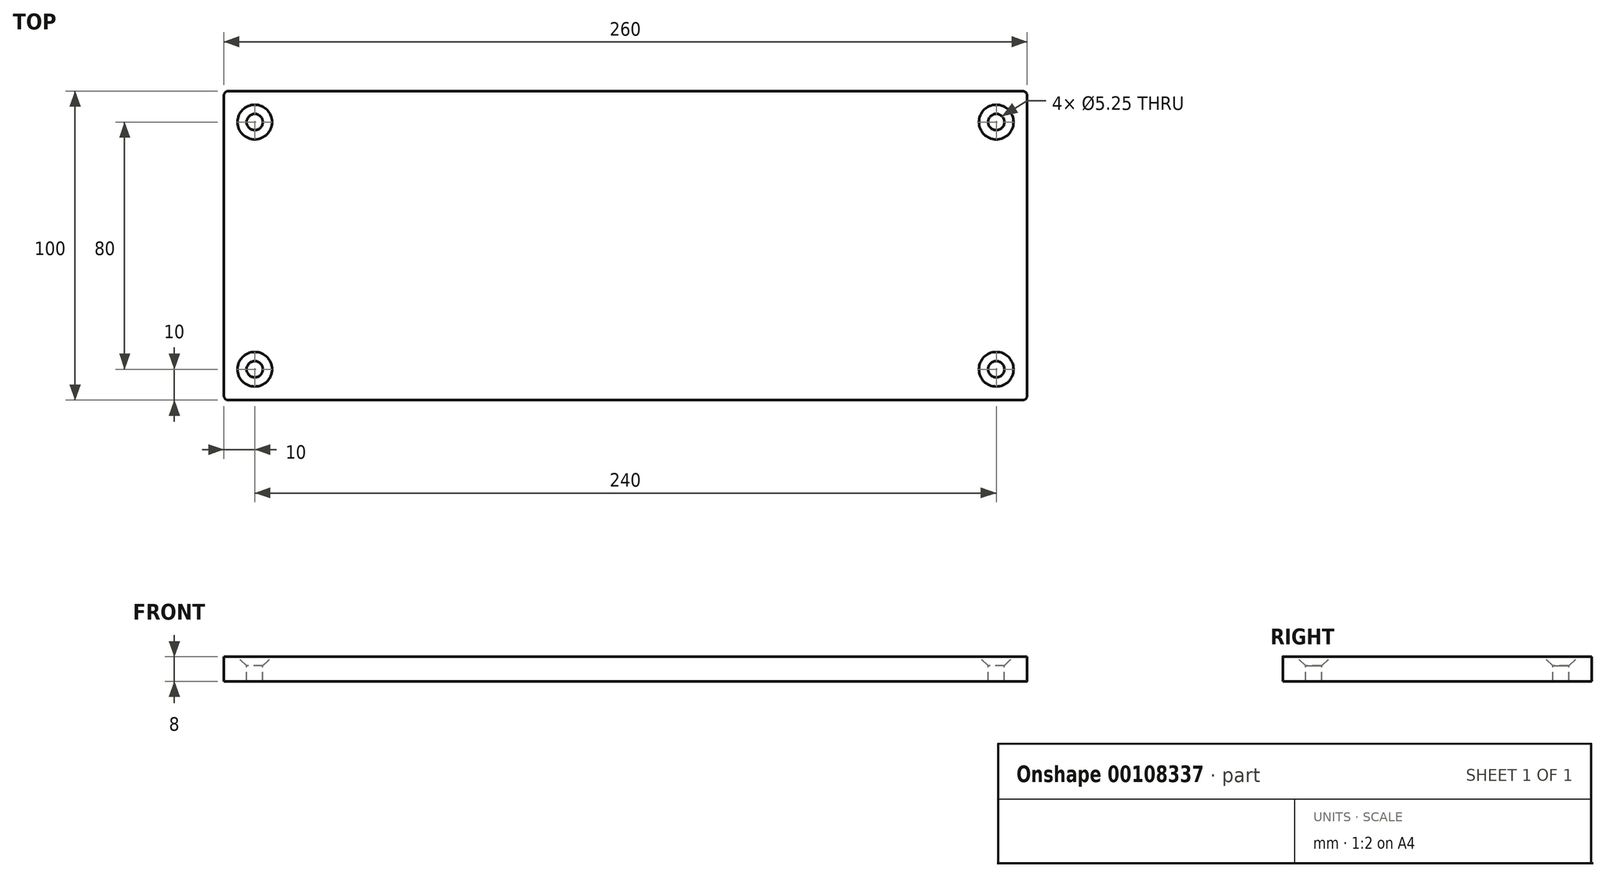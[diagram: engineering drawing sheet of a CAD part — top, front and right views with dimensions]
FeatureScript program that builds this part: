
annotation { "Feature Type Name" : "Feature", "Feature Type Description" : "" }
export const myFeature = defineFeature(function(context is Context, id is Id, definition is map)
    precondition{}
    {
        {
            var Q0;
            Q0=qCreatedBy(makeId("Top.planeOp"),FACE);
            var sketch = newSketch(context, id + "F0", { "sketchPlane" : qUnion([Q0])});
            skLineSegment(sketch, "E0.bottom", {"start": v(0, 0) * mm, "end": v(-260, 0) * mm});
            skLineSegment(sketch, "E0.top", {"start": v(0, 100) * mm, "end": v(-260, 100) * mm});
            skLineSegment(sketch, "E0.left", {"start": v(0, 0) * mm, "end": v(0, 100) * mm});
            skLineSegment(sketch, "E0.right", {"start": v(-260, 0) * mm, "end": v(-260, 100) * mm});
            skLineSegment(sketch, "E1", {"start": v(-260, 50) * mm, "end": v(0, 50) * mm, "construction": true});
            skLineSegment(sketch, "E2", {"start": v(-130, 100) * mm, "end": v(-130, 0) * mm, "construction": true});
            skPoint(sketch, "E3", {"position": v(-250, 10) * mm});
            skPoint(sketch, "E4.MirrorP", {"position": v(-250, 90) * mm});
            skPoint(sketch, "E5.MirrorP", {"position": v(-10, 90) * mm});
            skPoint(sketch, "E6.MirrorP", {"position": v(-10, 10) * mm});
            skSolve(sketch);
        }
        {
            var Q0;
            Q0=makeQuery(id+"F0.imprint","IMPRINT",FACE,{"disambiguationData":[TD([[makeQuery(id+"F0.imprint","IMPRINT",EDGE,{"derivedFrom":sQuery(id+"F0.wireOp",EDGE,"E0.bottom")}),-1.0]])]});
            extrude(context, id + "F1", {"entities" : qUnion([Q0]), "oppositeDirection" : true, "depth" : 8 * mm});
        }
        {
            var Q0;
            Q0=sQuery(id+"F0.wireOp",VERTEX,"E3");
            var Q1;
            Q1=sQuery(id+"F0.wireOp",VERTEX,"cffc4b24-a0ba-456e-b655-3c8573d52c1b");
            var Q2;
            Q2=sQuery(id+"F0.wireOp",VERTEX,"e33c571e-dceb-4edd-b5c1-62c351230e5a2.MirrorP");
            var Q3;
            Q3=sQuery(id+"F0.wireOp",VERTEX,"E6.MirrorP");
            var Q4;
            Q4=sQuery(id+"F0.wireOp",VERTEX,"e33c571e-dceb-4edd-b5c1-62c351230e5a3.MirrorP");
            var Q5;
            Q5=sQuery(id+"F0.wireOp",VERTEX,"E5.MirrorP");
            var Q6;
            Q6=sQuery(id+"F0.wireOp",VERTEX,"E4.MirrorP");
            var Q7;
            Q7=sQuery(id+"F0.wireOp",VERTEX,"1f4b834b-5920-4e6c-9070-407c551c4e2a0.MirrorP");
            var Q8;
            Q8=makeQuery(id+"F1.opExtrude","SWEPT_BODY",BODY,{"disambiguationData":[OSD([sQuery(id+"F0.wireOp",EDGE,"E0.bottom"),sQuery(id+"F0.wireOp",EDGE,"E0.top"),sQuery(id+"F0.wireOp",EDGE,"E0.left"),sQuery(id+"F0.wireOp",EDGE,"E0.right")])]});
            hole(context, id + "F2", {"style" : HoleStyle.C_SINK, "endStyle" : HoleEndStyle.THROUGH, "standardTappedOrClearance" : lookupTablePath({ "standard" : "ISO", "fit" : "Close", "size" : "M5", "type" : "Clearance" }), "standardBlindInLast" : lookupTablePath({ "fit" : "Close", "standard" : "ISO", "size" : "M5", "type" : "Clearance" }), "holeDiameter" : 5.25 * mm, "cSinkDiameter" : 11.2 * mm, "cSinkAngle" : 90 * degree, "locations" : qUnion([Q0, Q1, Q2, Q3, Q4, Q5, Q6, Q7]), "scope" : qUnion([Q8]), "isTappedThrough" : true});
        }
        {
            var Q0;
            Q0=makeQuery(id+"F1.opExtrude","SWEPT_EDGE",EDGE,{"disambiguationData":[OSD([sQuery(id+"F0.wireOp",EDGE,"E0.bottom"),sQuery(id+"F0.wireOp",EDGE,"E0.left")])]});
            var Q1;
            Q1=makeQuery(id+"F1.opExtrude","SWEPT_EDGE",EDGE,{"disambiguationData":[OSD([sQuery(id+"F0.wireOp",EDGE,"E0.top"),sQuery(id+"F0.wireOp",EDGE,"E0.left")])]});
            var Q2;
            Q2=makeQuery(id+"F1.opExtrude","SWEPT_EDGE",EDGE,{"disambiguationData":[OSD([sQuery(id+"F0.wireOp",EDGE,"E0.bottom"),sQuery(id+"F0.wireOp",EDGE,"E0.right")])]});
            var Q3;
            Q3=makeQuery(id+"F1.opExtrude","SWEPT_EDGE",EDGE,{"disambiguationData":[OSD([sQuery(id+"F0.wireOp",EDGE,"E0.top"),sQuery(id+"F0.wireOp",EDGE,"E0.right")])]});
            fillet(context, id + "F3", {"entities" : qUnion([Q0, Q1, Q2, Q3]), "radius" : 1.5 * mm, "tangentPropagation" : true, "allowEdgeOverflow" : false});
        }
    });
